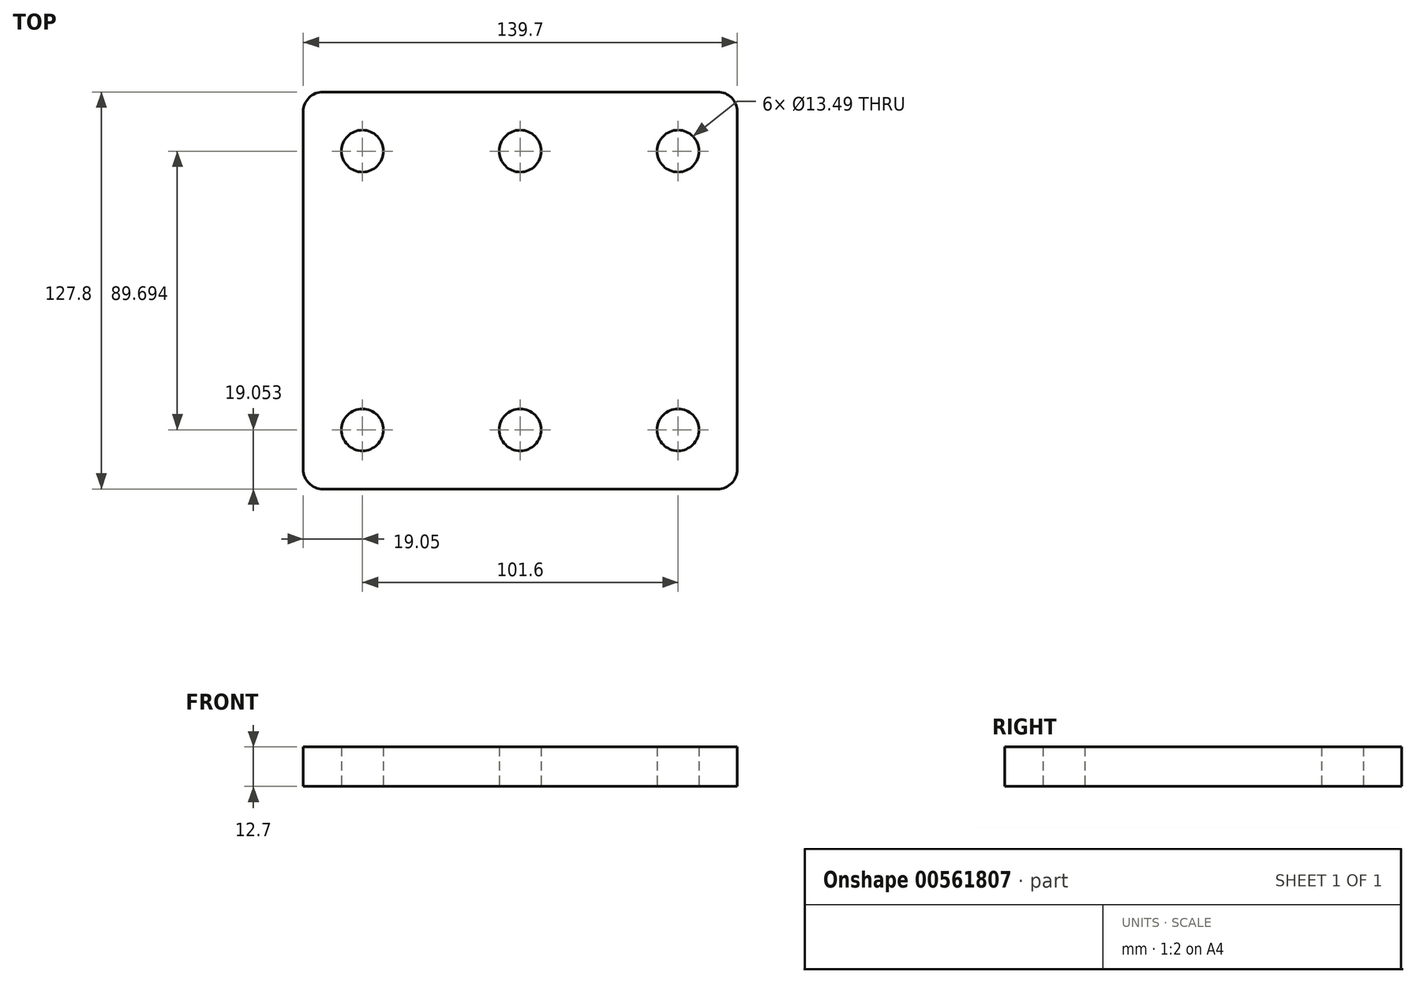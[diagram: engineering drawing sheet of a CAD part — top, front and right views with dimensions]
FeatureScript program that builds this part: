
annotation { "Feature Type Name" : "Feature", "Feature Type Description" : "" }
export const myFeature = defineFeature(function(context is Context, id is Id, definition is map)
    precondition{}
    {
        {
            var Q0;
            Q0=qCreatedBy(makeId("Top.planeOp"),FACE);
            cPlane(context, id + "F0", {"entities" : qUnion([Q0]), "cplaneType" : CPlaneType.OFFSET, "offset" : 25.4 * mm, "width" : 152.4 * mm, "height" : 152.4 * mm});
        }
        {
            var Q0;
            Q0=qCreatedBy(id+"F0.planeOp",FACE);
            var sketch = newSketch(context, id + "F1", { "sketchPlane" : qUnion([Q0])});
            skLineSegment(sketch, "E0.top", {"start": v(-50.8, -44.85) * mm, "end": v(50.8, -44.85) * mm, "construction": true});
            skLineSegment(sketch, "E0.left", {"start": v(-50.8, 44.85) * mm, "end": v(-50.8, -44.85) * mm, "construction": true});
            skCircle(sketch, "E1", {"center": v(-50.8, 44.85) * mm, "radius": 6.75 * mm});
            skCircle(sketch, "E2", {"center": v(50.8, 44.85) * mm, "radius": 6.75 * mm});
            skCircle(sketch, "E3", {"center": v(50.8, -44.85) * mm, "radius": 6.75 * mm});
            skCircle(sketch, "E4", {"center": v(-50.8, -44.85) * mm, "radius": 6.75 * mm});
            skLineSegment(sketch, "E5.bottom", {"start": v(-63.5, 63.9) * mm, "end": v(63.5, 63.9) * mm});
            skLineSegment(sketch, "E5.top", {"start": v(-63.5, -63.9) * mm, "end": v(63.5, -63.9) * mm});
            skLineSegment(sketch, "E5.left", {"start": v(-69.85, 57.55) * mm, "end": v(-69.85, -57.55) * mm});
            skLineSegment(sketch, "E5.right", {"start": v(69.85, 57.55) * mm, "end": v(69.85, -57.55) * mm});
            skPoint(sketch, "E6", {"position": v(50.8, 38.1) * mm});
            skPoint(sketch, "E7", {"position": v(50.8, -38.1) * mm});
            skPoint(sketch, "E8.visualSharp", {"position": v(69.85, 63.9) * mm});
            skArc(sketch, "E8.filletArc", {"start": v(69.85, 57.55) * mm, "mid": v(68, 62.04) * mm, "end": v(63.5, 63.9) * mm});
            skPoint(sketch, "E9.visualSharp", {"position": v(69.85, -63.9) * mm});
            skArc(sketch, "E9.filletArc", {"start": v(63.5, -63.9) * mm, "mid": v(68, -62.04) * mm, "end": v(69.85, -57.55) * mm});
            skPoint(sketch, "E10.visualSharp", {"position": v(-69.85, -63.9) * mm});
            skArc(sketch, "E10.filletArc", {"start": v(-69.85, -57.55) * mm, "mid": v(-68, -62.04) * mm, "end": v(-63.5, -63.9) * mm});
            skPoint(sketch, "E11.visualSharp", {"position": v(-69.85, 63.9) * mm});
            skArc(sketch, "E11.filletArc", {"start": v(-63.5, 63.9) * mm, "mid": v(-68, 62.04) * mm, "end": v(-69.85, 57.55) * mm});
            skLineSegment(sketch, "E12", {"start": v(50.8, 44.85) * mm, "end": v(50.8, 0) * mm, "construction": true});
            skLineSegment(sketch, "E13", {"start": v(50.8, 0) * mm, "end": v(50.8, -44.85) * mm, "construction": true});
            skLineSegment(sketch, "E14", {"start": v(-50.8, 44.85) * mm, "end": v(0, 44.85) * mm, "construction": true});
            skLineSegment(sketch, "E15", {"start": v(0, 44.85) * mm, "end": v(50.8, 44.85) * mm, "construction": true});
            skCircle(sketch, "E16", {"center": v(0, 44.85) * mm, "radius": 6.75 * mm});
            skCircle(sketch, "E17", {"center": v(0, -44.85) * mm, "radius": 6.75 * mm});
            skLineSegment(sketch, "E18", {"start": v(0, 44.85) * mm, "end": v(0, 63.9) * mm, "construction": true});
            skLineSegment(sketch, "E19", {"start": v(0, -44.85) * mm, "end": v(0, -63.9) * mm, "construction": true});
            skLineSegment(sketch, "E20", {"start": v(-50.8, 0) * mm, "end": v(-69.85, 0) * mm, "construction": true});
            skLineSegment(sketch, "E21", {"start": v(50.8, 0) * mm, "end": v(69.85, 0) * mm, "construction": true});
            skSolve(sketch);
        }
        {
            var Q0;
            Q0=makeQuery(id+"F1.imprint","IMPRINT",FACE,{"disambiguationData":[TD([[makeQuery(id+"F1.imprint","IMPRINT",EDGE,{"derivedFrom":sQuery(id+"F1.wireOp",EDGE,"E1")}),-1.0]])]});
            extrude(context, id + "F2", {"entities" : qUnion([Q0]), "depth" : 12.7 * mm, "offsetDistance" : 25.4 * mm});
        }
    });
